# Revit family: CoolBox k 2.0-7.0
name_source: partatom
category: Оборудование
units: mm (PartAtom-declared; Revit-internal decimal feet)

## family parameters
Всегда вертикально = Нет
Классификация = Нет
На основе рабочей плоскости = Нет
Общий = Нет
При загрузке вырезать с полостями = Нет
Размер круглого соединителя = Использовать диаметр
Тип детали = Нормальный
Точка расчета площади = Нет

## types (5) — shared parameters
ADSK_Количество фаз = 1
ADSK_Напряжение = 0 В
ВК от в края = 215 мм
Вентилятор от края = 215 мм
Высота ВК = 170 мм
Высота НК = 195 мм
Крепеж длина = 50 мм
Крепеж от края = 85 мм
НК от н края = 35 мм
Толщина НК = 70 мм
Фреон = R410A
выдавл_вент = 5 мм
zero-valued in all types: ADSK_Количество

## per-type parameters (varying)
| type | A Высота | ADSK_Масса | ADSK_Номинальная мощность | ADSK_Холодильная мощность | B Ширина | C Толщина | Фреон г | Фреон ж |
| CoolBox k 2.5 | 500 мм | 24 | 850 Вт | 2500 Вт | 600 мм | 230 мм | 9 мм | 6 мм |
| CoolBox k 2.0 | 500 мм | 23 | 700 Вт | 2000 Вт | 600 мм | 230 мм | 9 мм | 6 мм |
| CoolBox k 3.5 | 552 мм | 30 | 1130 Вт | 3500 Вт | 700 мм | 256 мм | 9 мм | 6 мм |
| CoolBox k 5.0 | 552 мм | 37 | 1710 Вт | 5000 Вт | 760 мм | 256 мм | 13 мм | 6 мм |
| CoolBox k 7.0 | 650 мм | 50 | 2280 Вт | 7000 Вт | 902 мм | 307 мм | 15 мм | 10 мм |

note: column(s) folded — value = type name in every type: ADSK_Наименование
